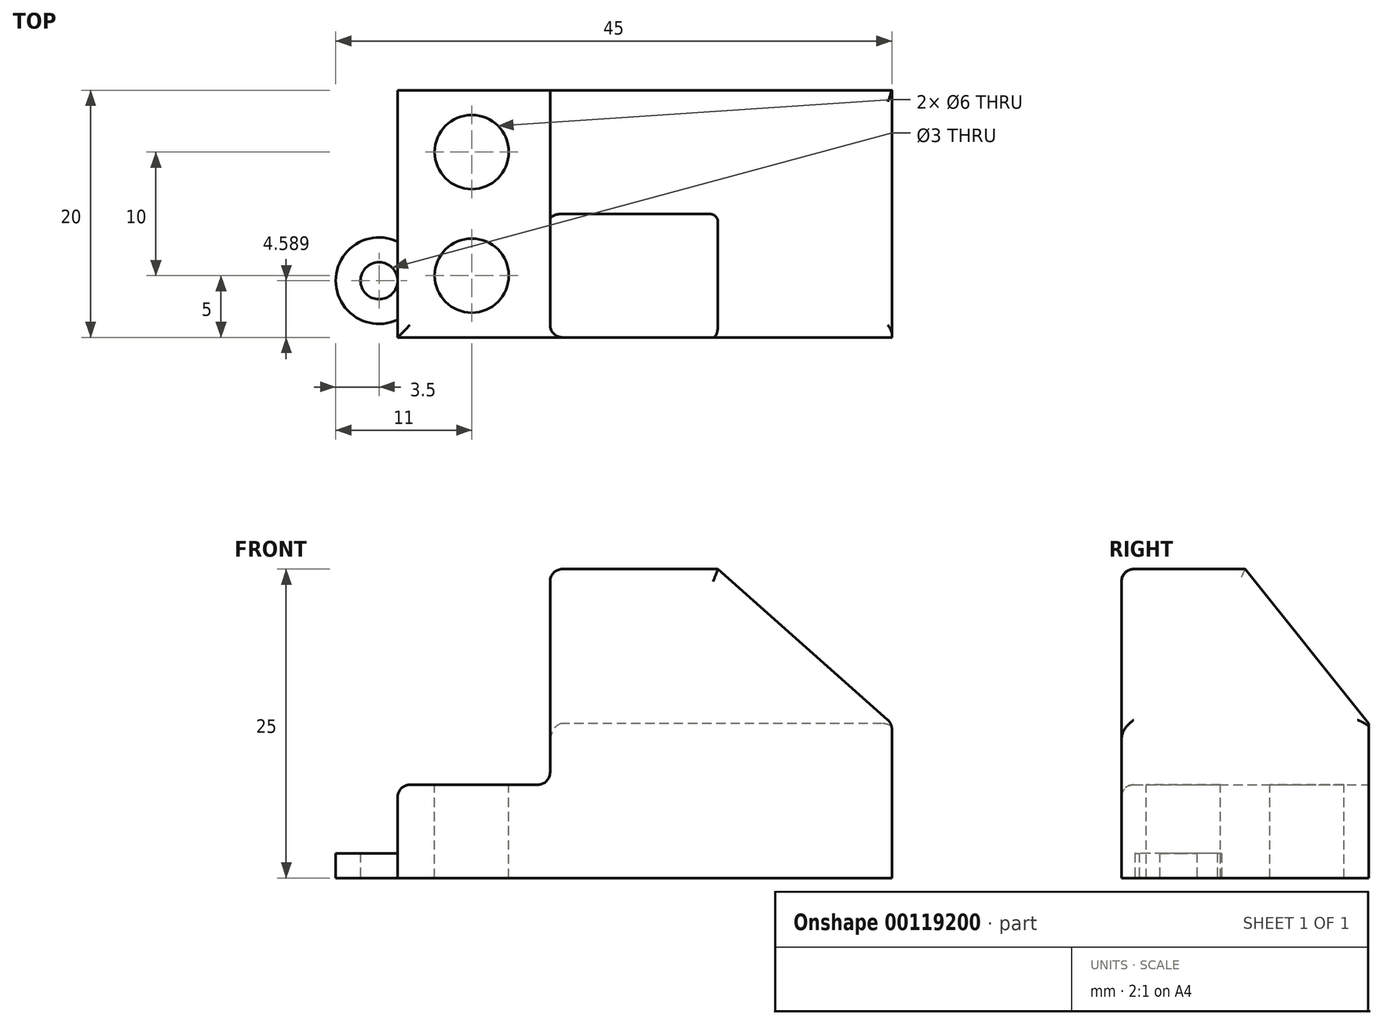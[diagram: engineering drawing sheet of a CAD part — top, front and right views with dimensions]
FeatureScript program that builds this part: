
annotation { "Feature Type Name" : "Feature", "Feature Type Description" : "" }
export const myFeature = defineFeature(function(context is Context, id is Id, definition is map)
    precondition{}
    {
        {
            var Q0;
            Q0=qCreatedBy(makeId("Top.planeOp"),FACE);
            var sketch = newSketch(context, id + "F0", { "sketchPlane" : qUnion([Q0])});
            skLineSegment(sketch, "E0.bottom", {"start": v(20, 10) * mm, "end": v(-20, 10) * mm});
            skLineSegment(sketch, "E0.top", {"start": v(20, -10) * mm, "end": v(-20, -10) * mm});
            skLineSegment(sketch, "E0.left", {"start": v(20, 10) * mm, "end": v(20, -10) * mm});
            skLineSegment(sketch, "E0.right", {"start": v(-20, 10) * mm, "end": v(-20, -10) * mm});
            skPoint(sketch, "E0.middle", {"position": v(0, 0) * mm});
            skSolve(sketch);
        }
        {
            var Q0;
            Q0=makeQuery(id+"F0.imprint","IMPRINT",FACE,{"disambiguationData":[TD([[makeQuery(id+"F0.imprint","IMPRINT",EDGE,{"derivedFrom":sQuery(id+"F0.wireOp",EDGE,"E0.bottom")}),1.0]])]});
            extrude(context, id + "F1", {"entities" : qUnion([Q0]), "depth" : 25 * mm});
        }
        {
            var Q0;
            Q0=makeQuery(id+"F1.opExtrude","SWEPT_FACE",FACE,{"disambiguationData":[OSD([sQuery(id+"F0.wireOp",EDGE,"E0.right")])]});
            var sketch = newSketch(context, id + "F2", { "sketchPlane" : qUnion([Q0])});
            skLineSegment(sketch, "E1", {"start": v(0, 25) * mm, "end": v(-10, 12.5) * mm});
            skLineSegment(sketch, "E2", {"start": v(-10, 12.5) * mm, "end": v(-10, 25) * mm});
            skLineSegment(sketch, "E3", {"start": v(-10, 25) * mm, "end": v(0, 25) * mm});
            skSolve(sketch);
        }
        {
            var Q0;
            Q0=makeQuery(id+"F2.imprint","IMPRINT",FACE,{"disambiguationData":[TD([[makeQuery(id+"F2.imprint","IMPRINT",EDGE,{"derivedFrom":sQuery(id+"F2.wireOp",EDGE,"E1")}),-1.0]])]});
            extrude(context, id + "F3", {"entities" : qUnion([Q0]), "operationType" : NewBodyOperationType.REMOVE, "oppositeDirection" : true, "depth" : 50.28 * mm});
        }
        {
            var Q0;
            Q0=makeQuery(id+"F1.opExtrude","SWEPT_FACE",FACE,{"disambiguationData":[OSD([sQuery(id+"F0.wireOp",EDGE,"E0.bottom")])]});
            cPlane(context, id + "F4", {"entities" : qUnion([Q0]), "cplaneType" : CPlaneType.OFFSET, "offset" : 0 * mm, "width" : 150 * mm, "height" : 150 * mm});
        }
        {
            var Q0;
            Q0=qCreatedBy(id+"F4.planeOp",FACE);
            var sketch = newSketch(context, id + "F5", { "sketchPlane" : qUnion([Q0])});
            skLineSegment(sketch, "E4", {"start": v(-20.05, 12.45) * mm, "end": v(-5.92, 25) * mm});
            skLineSegment(sketch, "E5", {"start": v(-5.92, 25) * mm, "end": v(-20, 25) * mm});
            skLineSegment(sketch, "E6", {"start": v(-20, 25) * mm, "end": v(-20.05, 12.45) * mm});
            skSolve(sketch);
        }
        {
            var Q0;
            Q0=makeQuery(id+"F5.imprint","IMPRINT",FACE,{"disambiguationData":[TD([[makeQuery(id+"F5.imprint","IMPRINT",EDGE,{"derivedFrom":sQuery(id+"F5.wireOp",EDGE,"E4")}),1.0]])]});
            extrude(context, id + "F6", {"entities" : qUnion([Q0]), "operationType" : NewBodyOperationType.REMOVE, "oppositeDirection" : true, "depth" : 40.3 * mm});
        }
        {
            var Q0;
            Q0=qCreatedBy(makeId("Top.planeOp"),FACE);
            var sketch = newSketch(context, id + "F7", { "sketchPlane" : qUnion([Q0])});
            skCircle(sketch, "E7", {"center": v(-21.5, -5.41) * mm, "radius": 3.5 * mm});
            skCircle(sketch, "E8", {"center": v(-21.5, -5.41) * mm, "radius": 1.5 * mm});
            skSolve(sketch);
        }
        {
            var Q0;
            Q0 = qSketchRegion(id + "F7", true);
            extrude(context, id + "F8", {"entities" : qUnion([Q0]), "operationType" : NewBodyOperationType.ADD, "depth" : 2 * mm});
        }
        {
            var Q0;
            Q0=qCreatedBy(id+"F4.planeOp",FACE);
            var sketch = newSketch(context, id + "F9", { "sketchPlane" : qUnion([Q0])});
            skLineSegment(sketch, "E9", {"start": v(7.66, 25.07) * mm, "end": v(7.66, 7.54) * mm});
            skLineSegment(sketch, "E10", {"start": v(7.66, 7.54) * mm, "end": v(21.76, 7.54) * mm});
            skLineSegment(sketch, "E11", {"start": v(21.76, 7.54) * mm, "end": v(21.76, 25.07) * mm});
            skLineSegment(sketch, "E12", {"start": v(21.76, 25.07) * mm, "end": v(7.66, 25.07) * mm});
            skSolve(sketch);
        }
        {
            var Q0;
            Q0 = qSketchRegion(id + "F9", true);
            extrude(context, id + "F10", {"entities" : qUnion([Q0]), "operationType" : NewBodyOperationType.REMOVE, "oppositeDirection" : true, "depth" : 44.5 * mm});
        }
        {
            var Q0;
            Q0=makeQuery(id+"F10.boolean.opBoolean","COPY",FACE,{"derivedFrom":makeQuery(id+"F10.opExtrude","SWEPT_FACE",FACE,{"disambiguationData":[OSD([sQuery(id+"F9.wireOp",EDGE,"E10")])]})});
            var sketch = newSketch(context, id + "F11", { "sketchPlane" : qUnion([Q0])});
            skCircle(sketch, "E13", {"center": v(-14, -5) * mm, "radius": 3 * mm});
            skPoint(sketch, "E13.centerSnap0", {"position": v(-20, 0) * mm});
            skCircle(sketch, "E14", {"center": v(-14, 5) * mm, "radius": 3 * mm});
            skSolve(sketch);
        }
        {
            var Q0;
            Q0 = qSketchRegion(id + "F11", true);
            extrude(context, id + "F12", {"entities" : qUnion([Q0]), "operationType" : NewBodyOperationType.REMOVE, "oppositeDirection" : true, "depth" : 25 * mm});
        }
        {
            var Q0;
            Q0=makeQuery(id+"F6.boolean.opBoolean","INTERSECT",EDGE,{"derivedFrom":[makeQuery(id+"F3.boolean.opBoolean","COPY",FACE,{"derivedFrom":makeQuery(id+"F3.opExtrude","SWEPT_FACE",FACE,{"disambiguationData":[OSD([sQuery(id+"F2.wireOp",EDGE,"E1")])]})}),makeQuery(id+"F6.opExtrude","SWEPT_FACE",FACE,{"disambiguationData":[OSD([sQuery(id+"F5.wireOp",EDGE,"E4")])]})]});
            var Q1;
            Q1=makeQuery(id+"F3.boolean.opBoolean","COPY",EDGE,{"derivedFrom":makeQuery(id+"F3.opExtrude","SWEPT_EDGE",EDGE,{"disambiguationData":[OSD([sQuery(id+"F0.wireOp",EDGE,"E0.right"),sQuery(id+"F2.wireOp",EDGE,"E1"),sQuery(id+"F2.wireOp",EDGE,"E3")])]})});
            var Q2;
            Q2=makeQuery(id+"F3.boolean.opBoolean","COPY",EDGE,{"derivedFrom":makeQuery(id+"F3.opExtrude","SWEPT_EDGE",EDGE,{"disambiguationData":[OSD([sQuery(id+"F0.wireOp",EDGE,"E0.bottom"),sQuery(id+"F0.wireOp",EDGE,"E0.right"),sQuery(id+"F2.wireOp",EDGE,"E1"),sQuery(id+"F2.wireOp",EDGE,"E2")])]})});
            var Q3;
            Q3=makeQuery(id+"F10.boolean.opBoolean","INTERSECT",EDGE,{"derivedFrom":[makeQuery(id+"F3.boolean.opBoolean","COPY",FACE,{"derivedFrom":makeQuery(id+"F3.opExtrude","SWEPT_FACE",FACE,{"disambiguationData":[OSD([sQuery(id+"F2.wireOp",EDGE,"E1")])]})}),makeQuery(id+"F10.opExtrude","SWEPT_FACE",FACE,{"disambiguationData":[OSD([sQuery(id+"F9.wireOp",EDGE,"E9")])]})]});
            var Q4;
            Q4=makeQuery(id+"F10.boolean.opBoolean","COPY",EDGE,{"derivedFrom":makeQuery(id+"F10.opExtrude","CAP_EDGE",EDGE,{"disambiguationData":[OSD([sQuery(id+"F9.wireOp",EDGE,"E9")])],"isStart":true})});
            var Q5;
            Q5=makeQuery(id+"F10.boolean.opBoolean","COPY",EDGE,{"derivedFrom":makeQuery(id+"F10.opExtrude","CAP_EDGE",EDGE,{"disambiguationData":[OSD([sQuery(id+"F9.wireOp",EDGE,"E10")])],"isStart":true})});
            var Q6;
            Q6=makeQuery(id+"F10.boolean.opBoolean","INTERSECT",EDGE,{"derivedFrom":[makeQuery(id+"F1.opExtrude","SWEPT_FACE",FACE,{"disambiguationData":[OSD([sQuery(id+"F0.wireOp",EDGE,"E0.right")])]}),makeQuery(id+"F10.opExtrude","SWEPT_FACE",FACE,{"disambiguationData":[OSD([sQuery(id+"F9.wireOp",EDGE,"E10")])]})]});
            var Q7;
            Q7=makeQuery(id+"F6.boolean.opBoolean","INTERSECT",EDGE,{"derivedFrom":[makeQuery(id+"F1.opExtrude","SWEPT_FACE",FACE,{"disambiguationData":[OSD([sQuery(id+"F0.wireOp",EDGE,"E0.top")])]}),makeQuery(id+"F6.opExtrude","SWEPT_FACE",FACE,{"disambiguationData":[OSD([sQuery(id+"F5.wireOp",EDGE,"E4")])]})]});
            var Q8;
            Q8=makeQuery(id+"F6.boolean.opBoolean","COPY",EDGE,{"derivedFrom":makeQuery(id+"F6.opExtrude","SWEPT_EDGE",EDGE,{"disambiguationData":[OSD([sQuery(id+"F5.wireOp",EDGE,"E4"),sQuery(id+"F5.wireOp",EDGE,"E5")])]})});
            var Q9;
            Q9=makeQuery(id+"F1.opExtrude","CAP_EDGE",EDGE,{"disambiguationData":[OSD([sQuery(id+"F0.wireOp",EDGE,"E0.top")])],"isStart":false});
            var Q10;
            Q10=makeQuery(id+"F10.boolean.opBoolean","INTERSECT",EDGE,{"derivedFrom":[makeQuery(id+"F1.opExtrude","SWEPT_FACE",FACE,{"disambiguationData":[OSD([sQuery(id+"F0.wireOp",EDGE,"E0.top")])]}),makeQuery(id+"F10.opExtrude","SWEPT_FACE",FACE,{"disambiguationData":[OSD([sQuery(id+"F9.wireOp",EDGE,"E9")])]})]});
            var Q11;
            Q11=makeQuery(id+"F10.boolean.opBoolean","INTERSECT",EDGE,{"derivedFrom":[makeQuery(id+"F1.opExtrude","CAP_FACE",FACE,{"disambiguationData":[OSD([sQuery(id+"F0.wireOp",EDGE,"E0.bottom"),sQuery(id+"F0.wireOp",EDGE,"E0.top"),sQuery(id+"F0.wireOp",EDGE,"E0.left"),sQuery(id+"F0.wireOp",EDGE,"E0.right")])],"isStart":false}),makeQuery(id+"F10.opExtrude","SWEPT_FACE",FACE,{"disambiguationData":[OSD([sQuery(id+"F9.wireOp",EDGE,"E9")])]})]});
            var Q12;
            Q12=makeQuery(id+"F10.boolean.opBoolean","INTERSECT",EDGE,{"derivedFrom":[makeQuery(id+"F1.opExtrude","SWEPT_FACE",FACE,{"disambiguationData":[OSD([sQuery(id+"F0.wireOp",EDGE,"E0.top")])]}),makeQuery(id+"F10.opExtrude","SWEPT_FACE",FACE,{"disambiguationData":[OSD([sQuery(id+"F9.wireOp",EDGE,"E10")])]})]});
            var Q13;
            Q13=makeQuery(id+"F10.boolean.opBoolean","COPY",EDGE,{"derivedFrom":makeQuery(id+"F10.opExtrude","SWEPT_EDGE",EDGE,{"disambiguationData":[OSD([sQuery(id+"F9.wireOp",EDGE,"E9"),sQuery(id+"F9.wireOp",EDGE,"E10")])]})});
            var Q14;
            Q14=makeQuery(id+"F6.boolean.opBoolean","INTERSECT",EDGE,{"derivedFrom":[makeQuery(id+"F1.opExtrude","SWEPT_FACE",FACE,{"disambiguationData":[OSD([sQuery(id+"F0.wireOp",EDGE,"E0.left")])]}),makeQuery(id+"F6.opExtrude","SWEPT_FACE",FACE,{"disambiguationData":[OSD([sQuery(id+"F5.wireOp",EDGE,"E4")])]})]});
            fillet(context, id + "F13", {"entities" : qUnion([Q0, Q1, Q2, Q3, Q4, Q5, Q6, Q7, Q8, Q9, Q10, Q11, Q12, Q13, Q14]), "radius" : 1 * mm, "tangentPropagation" : true, "allowEdgeOverflow" : false});
        }
    });
